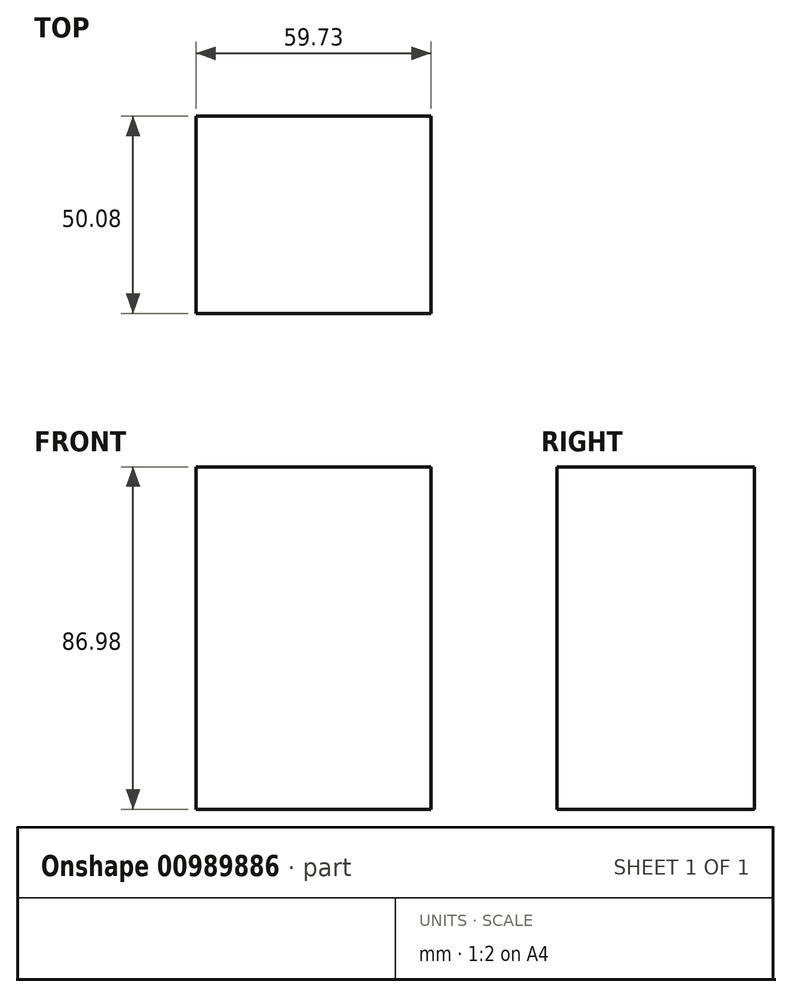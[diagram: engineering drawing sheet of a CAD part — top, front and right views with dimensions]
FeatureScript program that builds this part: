
annotation { "Feature Type Name" : "Feature", "Feature Type Description" : "" }
export const myFeature = defineFeature(function(context is Context, id is Id, definition is map)
    precondition{}
    {
        {
            var Q0;
            Q0=qCreatedBy(makeId("Right.planeOp"),FACE);
            var sketch = newSketch(context, id + "F0", { "sketchPlane" : qUnion([Q0])});
            skLineSegment(sketch, "E0.bottom", {"start": v(-34.69, 0) * mm, "end": v(15.39, 0) * mm});
            skLineSegment(sketch, "E0.top", {"start": v(-34.69, -86.98) * mm, "end": v(15.39, -86.98) * mm});
            skLineSegment(sketch, "E0.left", {"start": v(-34.69, 0) * mm, "end": v(-34.69, -86.98) * mm});
            skLineSegment(sketch, "E0.right", {"start": v(15.39, 0) * mm, "end": v(15.39, -86.98) * mm});
            skSolve(sketch);
        }
        {
            var Q0;
            Q0 = qSketchRegion(id + "F0", true);
            extrude(context, id + "F1", {"entities" : qUnion([Q0]), "oppositeDirection" : true, "depth" : 3.75 * mm, "offsetDistance" : 25.4 * mm});
        }
        {
            var Q0;
            Q0=makeQuery(id+"F1.opExtrude","CAP_FACE",FACE,{"disambiguationData":[OSD([sQuery(id+"F0.wireOp",EDGE,"E0.bottom"),sQuery(id+"F0.wireOp",EDGE,"E0.top"),sQuery(id+"F0.wireOp",EDGE,"E0.left"),sQuery(id+"F0.wireOp",EDGE,"E0.right")])],"isStart":false});
            var sketch = newSketch(context, id + "F2", { "sketchPlane" : qUnion([Q0])});
            skLineSegment(sketch, "E1.bottom", {"start": v(-10.7, 0) * mm, "end": v(30.33, 0) * mm});
            skLineSegment(sketch, "E1.top", {"start": v(-10.7, -82.46) * mm, "end": v(30.33, -82.46) * mm});
            skLineSegment(sketch, "E1.left", {"start": v(-10.7, 0) * mm, "end": v(-10.7, -82.46) * mm});
            skLineSegment(sketch, "E1.right", {"start": v(30.33, 0) * mm, "end": v(30.33, -82.46) * mm});
            skSolve(sketch);
        }
        {
            var Q0;
            Q0 = qSketchRegion(id + "F2", true);
            var Q1;
            Q1=makeQuery(id+"F2.imprint","IMPRINT",FACE,{"disambiguationData":[TD([[makeQuery(id+"F2.imprint","IMPRINT",EDGE,{"derivedFrom":sQuery(id+"F2.wireOp",EDGE,"E1.top")}),-1.0]])]});
            extrude(context, id + "F3", {"entities" : qUnion([Q0, Q1]), "operationType" : NewBodyOperationType.ADD, "depth" : 56 * mm, "offsetDistance" : 25.4 * mm});
        }
    });
